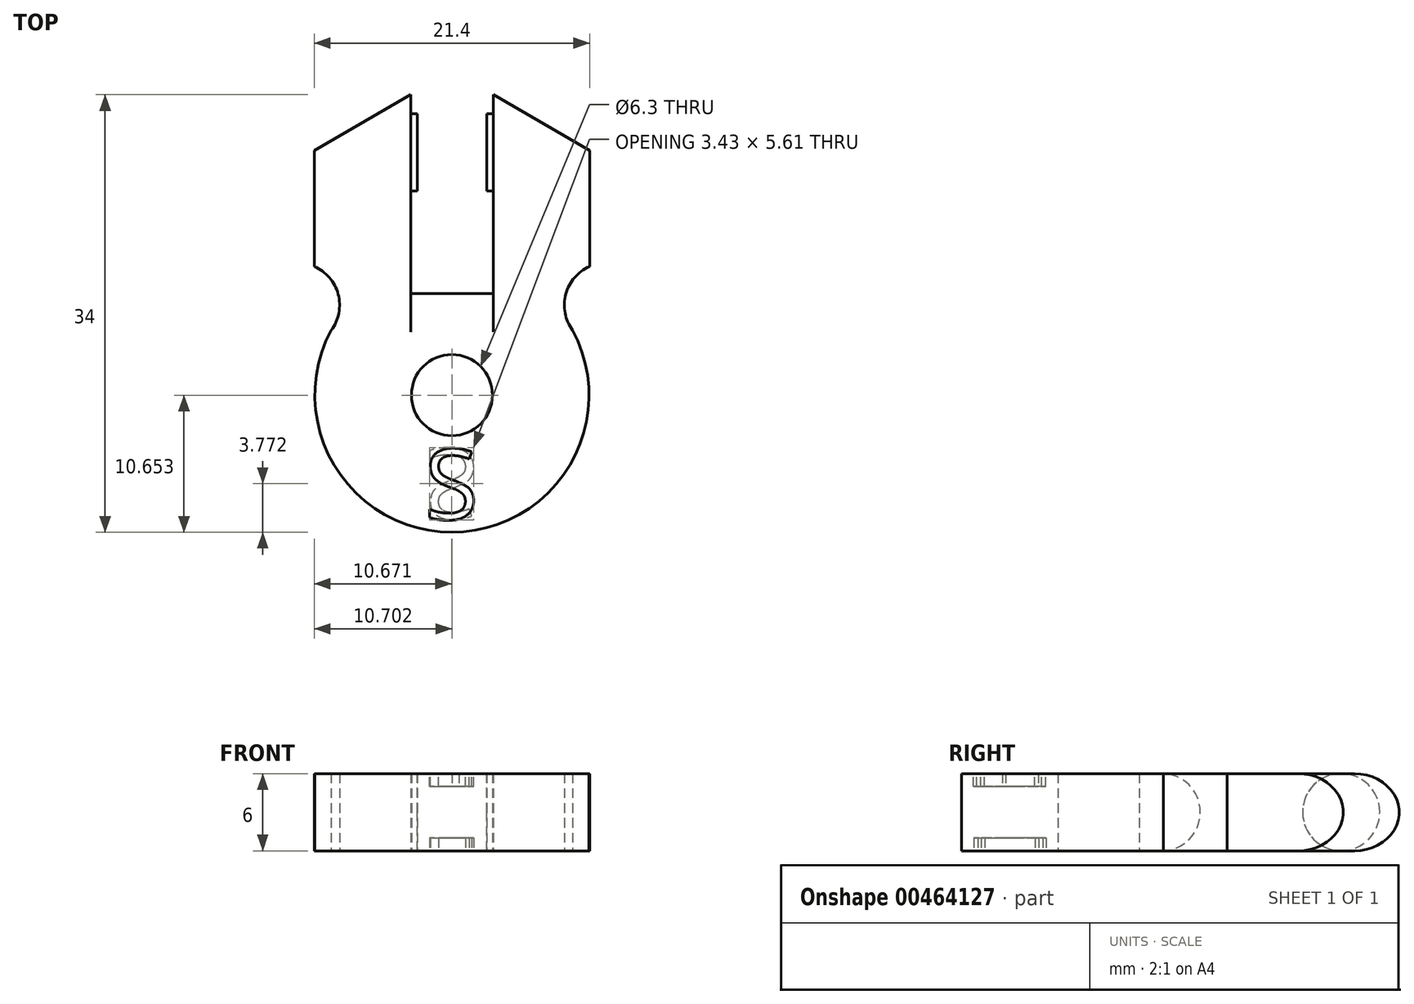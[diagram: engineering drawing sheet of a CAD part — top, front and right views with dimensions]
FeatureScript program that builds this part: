
annotation { "Feature Type Name" : "Feature", "Feature Type Description" : "" }
export const myFeature = defineFeature(function(context is Context, id is Id, definition is map)
    precondition{}
    {
        {
            var Q0;
            Q0=qCreatedBy(makeId("Top.planeOp"),FACE);
            var sketch = newSketch(context, id + "F0", { "sketchPlane" : qUnion([Q0])});
            skCircle(sketch, "E0", {"center": v(-10.56, -6.9) * mm, "radius": 10.65 * mm});
            skCircle(sketch, "E1", {"center": v(-10.56, -6.9) * mm, "radius": 3.15 * mm});
            skLineSegment(sketch, "E2", {"start": v(-10.56, -6.9) * mm, "end": v(-10.56, 3.74) * mm});
            skLineSegment(sketch, "E3", {"start": v(-13.76, 1.2) * mm, "end": v(-13.76, 16.44) * mm});
            skLineSegment(sketch, "E4", {"start": v(-7.36, 1.2) * mm, "end": v(-7.36, 16.44) * mm});
            skLineSegment(sketch, "E5", {"start": v(-7.36, 16.44) * mm, "end": v(0.14, 12.1) * mm});
            skLineSegment(sketch, "E6", {"start": v(-13.76, 16.44) * mm, "end": v(-21.26, 12.1) * mm});
            skLineSegment(sketch, "E7", {"start": v(-21.26, 12.1) * mm, "end": v(-21.26, 3.1) * mm});
            skLineSegment(sketch, "E8", {"start": v(0.14, 12.1) * mm, "end": v(0.14, 3.1) * mm});
            skLineSegment(sketch, "E9", {"start": v(-21.26, 12.1) * mm, "end": v(-21.26, 16.44) * mm});
            skLineSegment(sketch, "E10", {"start": v(-21.26, 16.44) * mm, "end": v(-13.76, 16.44) * mm});
            skArc(sketch, "E11", {"start": v(-19.94, -1.86) * mm, "mid": v(-19.4, 0.93) * mm, "end": v(-21.26, 3.1) * mm});
            skArc(sketch, "E12", {"start": v(0.14, 3.1) * mm, "mid": v(-1.72, 0.93) * mm, "end": v(-1.18, -1.86) * mm});
            skLineSegment(sketch, "E13", {"start": v(-13.76, 1.2) * mm, "end": v(-13.76, 1) * mm});
            skLineSegment(sketch, "E14", {"start": v(-13.76, 1) * mm, "end": v(-7.36, 1) * mm});
            skLineSegment(sketch, "E15", {"start": v(-7.36, 1) * mm, "end": v(-7.36, 1.2) * mm});
            skSolve(sketch);
        }
        {
            var Q0;
            {var subQ0=sQuery(id+"F0.wireOp",EDGE,"E6");Q0=makeQuery(id+"F0.imprint","IMPRINT",FACE,{"disambiguationData":[TD([[makeQuery(id+"F0.imprint","IMPRINT",EDGE,{"derivedFrom":subQ0}),1.0]])]});}
            var Q1;
            Q1=makeQuery(id+"F0.imprint","IMPRINT",FACE,{"disambiguationData":[TD([[makeQuery(id+"F0.imprint","IMPRINT",EDGE,{"derivedFrom":sQuery(id+"F0.wireOp",EDGE,"E1")}),-1.0]])]});
            var Q2;
            {var subQ1=sQuery(id+"F0.wireOp",EDGE,"E5");Q2=makeQuery(id+"F0.imprint","IMPRINT",FACE,{"disambiguationData":[TD([[makeQuery(id+"F0.imprint","IMPRINT",EDGE,{"derivedFrom":subQ1}),-1.0]])]});}
            extrude(context, id + "F1", {"entities" : qUnion([Q0, Q1, Q2]), "depth" : 6 * mm});
        }
        {
            var Q0;
            Q0=makeQuery(id+"F1.opExtrude","SWEPT_FACE",FACE,{"disambiguationData":[OSD([sQuery(id+"F0.wireOp",EDGE,"E3")])]});
            var sketch = newSketch(context, id + "F2", { "sketchPlane" : qUnion([Q0])});
            skCircle(sketch, "E16", {"center": v(11.94, 3) * mm, "radius": 3 * mm});
            skSolve(sketch);
        }
        {
            var Q0;
            {var subQ0=sQuery(id+"F2.wireOp",EDGE,"E16");var subQ1=sQuery(id+"F0.wireOp",EDGE,"E3");var subQ2=makeQuery(id+"F2.imprint","INTERSECT",VERTEX,{"derivedFrom":[makeQuery(id+"F1.opExtrude","CAP_EDGE",EDGE,{"disambiguationData":[OSD([subQ1])],"isStart":true}),subQ0]});Q0=makeQuery(id+"F2.imprint","IMPRINT",FACE,{"disambiguationData":[TD([[makeQuery(id+"F2.imprint","IMPRINT",EDGE,{"disambiguationData":[TD([[subQ2,1.0]])],"derivedFrom":subQ0}),1.0]])]});}
            extrude(context, id + "F3", {"entities" : qUnion([Q0]), "operationType" : NewBodyOperationType.ADD, "depth" : .5 * mm});
        }
        {
            var Q0;
            Q0=makeQuery(id+"F1.opExtrude","SWEPT_FACE",FACE,{"disambiguationData":[OSD([sQuery(id+"F0.wireOp",EDGE,"E4")])]});
            var sketch = newSketch(context, id + "F4", { "sketchPlane" : qUnion([Q0])});
            skCircle(sketch, "E17", {"center": v(-11.94, 3) * mm, "radius": 3 * mm});
            skSolve(sketch);
        }
        {
            var Q0;
            {var subQ0=sQuery(id+"F4.wireOp",EDGE,"E17");var subQ1=sQuery(id+"F0.wireOp",EDGE,"E4");var subQ2=makeQuery(id+"F4.imprint","INTERSECT",VERTEX,{"derivedFrom":[makeQuery(id+"F1.opExtrude","CAP_EDGE",EDGE,{"disambiguationData":[OSD([subQ1])],"isStart":true}),subQ0]});Q0=makeQuery(id+"F4.imprint","IMPRINT",FACE,{"disambiguationData":[TD([[makeQuery(id+"F4.imprint","IMPRINT",EDGE,{"disambiguationData":[TD([[subQ2,1.0]])],"derivedFrom":subQ0}),1.0]])]});}
            extrude(context, id + "F5", {"entities" : qUnion([Q0]), "operationType" : NewBodyOperationType.ADD, "depth" : .5 * mm});
        }
        {
            var Q0;
            Q0=makeQuery(id+"F1.opExtrude","CAP_EDGE",EDGE,{"disambiguationData":[OSD([sQuery(id+"F0.wireOp",EDGE,"E14")])],"isStart":true});
            var Q1;
            Q1=makeQuery(id+"F1.opExtrude","CAP_EDGE",EDGE,{"disambiguationData":[OSD([sQuery(id+"F0.wireOp",EDGE,"E14")])],"isStart":false});
            fillet(context, id + "F6", {"entities" : qUnion([Q0, Q1]), "radius" : 3 * mm, "tangentPropagation" : true, "allowEdgeOverflow" : false});
        }
        {
            var Q0;
            Q0=makeQuery(id+"F1.opExtrude","CAP_EDGE",EDGE,{"disambiguationData":[OSD([sQuery(id+"F0.wireOp",EDGE,"E5")])],"isStart":false});
            var Q1;
            Q1=makeQuery(id+"F1.opExtrude","CAP_EDGE",EDGE,{"disambiguationData":[OSD([sQuery(id+"F0.wireOp",EDGE,"E5")])],"isStart":true});
            var Q2;
            Q2=makeQuery(id+"F1.opExtrude","CAP_EDGE",EDGE,{"disambiguationData":[OSD([sQuery(id+"F0.wireOp",EDGE,"E6")])],"isStart":false});
            var Q3;
            Q3=makeQuery(id+"F1.opExtrude","CAP_EDGE",EDGE,{"disambiguationData":[OSD([sQuery(id+"F0.wireOp",EDGE,"E6")])],"isStart":true});
            fillet(context, id + "F7", {"entities" : qUnion([Q0, Q1, Q2, Q3]), "radius" : 3 * mm, "tangentPropagation" : true, "allowEdgeOverflow" : false});
        }
        {
            var Q0;
            Q0=makeQuery(id+"F1.opExtrude","CAP_FACE",FACE,{"disambiguationData":[OSD([sQuery(id+"F0.wireOp",EDGE,"E0"),sQuery(id+"F0.wireOp",EDGE,"E1"),sQuery(id+"F0.wireOp",EDGE,"E3"),sQuery(id+"F0.wireOp",EDGE,"E4"),sQuery(id+"F0.wireOp",EDGE,"E5"),sQuery(id+"F0.wireOp",EDGE,"E6"),sQuery(id+"F0.wireOp",EDGE,"E7"),sQuery(id+"F0.wireOp",EDGE,"E8"),sQuery(id+"F0.wireOp",EDGE,"E11"),sQuery(id+"F0.wireOp",EDGE,"E12"),sQuery(id+"F0.wireOp",EDGE,"E13"),sQuery(id+"F0.wireOp",EDGE,"E14"),sQuery(id+"F0.wireOp",EDGE,"E15")])],"isStart":false});
            var sketch = newSketch(context, id + "F8", { "sketchPlane" : qUnion([Q0])});
            skText(sketch, "E18", { "text": "S", "fontName": "OpenSans-Regular.ttf"});
            skCircle(sketch, "E19", {"center": v(-10.56, -6.9) * mm, "radius": 1.7 * mm});
            skLineSegment(sketch, "E20", {"start": v(-10.56, -6.9) * mm, "end": v(-10.54, -18.94) * mm});
            const initialGuessF8  = {"E18": [-0.0127, -0.01656, 1, 0, 0.0055]};
            skSetInitialGuess(sketch, initialGuessF8);
            skSolve(sketch);
        }
        {
            var Q0;
            {var subQ7=sQuery(id+"F8.wireOp",EDGE,"E18.sketch_text.stroke-0");Q0=makeQuery(id+"F8.imprint","IMPRINT",FACE,{"disambiguationData":[TD([[makeQuery(id+"F8.imprint","IMPRINT",EDGE,{"derivedFrom":subQ7}),-1.0]])]});}
            var Q1;
            {var subQ0=sQuery(id+"F8.wireOp",EDGE,"E18.sketch_text.stroke-2");Q1=makeQuery(id+"F8.imprint","IMPRINT",FACE,{"disambiguationData":[TD([[makeQuery(id+"F8.imprint","IMPRINT",EDGE,{"derivedFrom":subQ0}),-1.0]])]});}
            var Q2;
            {var subQ7=sQuery(id+"F8.wireOp",EDGE,"E18.sketch_text.stroke-11");Q2=makeQuery(id+"F8.imprint","IMPRINT",FACE,{"disambiguationData":[TD([[makeQuery(id+"F8.imprint","IMPRINT",EDGE,{"derivedFrom":subQ7}),-1.0]])]});}
            var Q3;
            {var subQ6=sQuery(id+"F8.wireOp",EDGE,"E18.sketch_text.stroke-15");Q3=makeQuery(id+"F8.imprint","IMPRINT",FACE,{"disambiguationData":[TD([[makeQuery(id+"F8.imprint","IMPRINT",EDGE,{"derivedFrom":subQ6}),-1.0]])]});}
            extrude(context, id + "F9", {"entities" : qUnion([Q0, Q1, Q2, Q3]), "operationType" : NewBodyOperationType.REMOVE, "oppositeDirection" : true, "depth" : 1 * mm, "offsetDistance" : 25 * mm});
        }
        {
            var Q0;
            Q0=makeQuery(id+"F1.opExtrude","CAP_FACE",FACE,{"disambiguationData":[OSD([sQuery(id+"F0.wireOp",EDGE,"E0"),sQuery(id+"F0.wireOp",EDGE,"E1"),sQuery(id+"F0.wireOp",EDGE,"E3"),sQuery(id+"F0.wireOp",EDGE,"E4"),sQuery(id+"F0.wireOp",EDGE,"E5"),sQuery(id+"F0.wireOp",EDGE,"E6"),sQuery(id+"F0.wireOp",EDGE,"E7"),sQuery(id+"F0.wireOp",EDGE,"E8"),sQuery(id+"F0.wireOp",EDGE,"E11"),sQuery(id+"F0.wireOp",EDGE,"E12"),sQuery(id+"F0.wireOp",EDGE,"E13"),sQuery(id+"F0.wireOp",EDGE,"E14"),sQuery(id+"F0.wireOp",EDGE,"E15")])],"isStart":true});
            var sketch = newSketch(context, id + "F10", { "sketchPlane" : qUnion([Q0])});
            skText(sketch, "E21", { "text": "S", "fontName": "OpenSans-Regular.ttf"});
            const initialGuessF10  = {"E21": [-0.0127, 0.01106, 1, 0, 0.0055]};
            skSetInitialGuess(sketch, initialGuessF10);
            skSolve(sketch);
        }
        {
            var Q0;
            Q0=makeQuery(id+"F10.imprint","IMPRINT",FACE,{"disambiguationData":[TD([[makeQuery(id+"F10.imprint","IMPRINT",EDGE,{"derivedFrom":sQuery(id+"F10.wireOp",EDGE,"E21.sketch_text.stroke-0")}),-1.0]])]});
            extrude(context, id + "F11", {"entities" : qUnion([Q0]), "operationType" : NewBodyOperationType.REMOVE, "oppositeDirection" : true, "depth" : 1 * mm, "offsetDistance" : 25 * mm});
        }
    });
